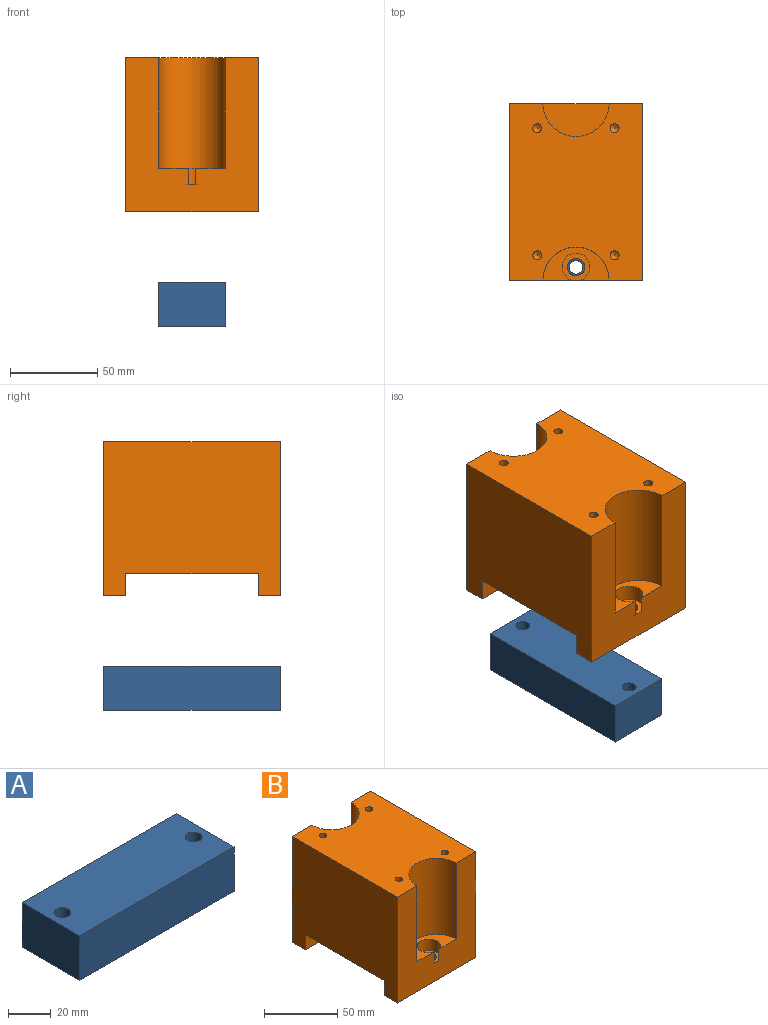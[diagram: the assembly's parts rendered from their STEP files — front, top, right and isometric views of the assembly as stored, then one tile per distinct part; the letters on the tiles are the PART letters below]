
ASSEMBLY  parts=2 mates=1
PART A: 8 faces, bbox 101.6x38.1x25.4 mm
  f0: plane 38.1x25.4mm, normal (-1,0,0), area 967.7mm2, adj f1,f3,f4,f5
  f1: plane 101.6x25.4mm, normal (0,-1,0), area 2580.6mm2, adj f0,f2,f4,f5
  f2: plane 38.1x25.4mm, normal (1,0,0), area 967.7mm2, adj f1,f3,f4,f5
  f3: plane 101.6x25.4mm, normal (0,1,0), area 2580.6mm2, adj f0,f2,f4,f5
  f4: plane 101.6x38.1mm, normal (0,0,1), area 3772mm2, adj f0,f1,f2,f3,f6,f7
  f5: plane 101.6x38.1mm, normal (0,0,-1), area 3772mm2, adj f0,f1,f2,f3,f6,f7
  f6: cylinder r=3.97mm len=25.4mm, axis (0,0,1), area 633.4mm2, adj f4,f5
  f7: cylinder r=3.97mm len=25.4mm, axis (0,0,1), area 633.4mm2, adj f4,f5
PART B: 25 faces, bbox 76.2x101.6x88.5 mm
  f0: plane 88.52x76.2mm, normal (0,-1,0), area 4283.5mm2, adj f1,f4,f5,f6,f9,f11,f14,f15
  f1: plane 38.1x19.05mm, normal (0,0,1), area 373.1mm2, adj f0,f9,f15
  f2: plane 76.2x76.2mm, normal (0,0,-1), area 5806.4mm2, adj f5,f6,f10,f12
  f3: plane 88.52x76.2mm, normal (0,1,0), area 4325.8mm2, adj f4,f5,f6,f7,f8,f13
  f4: plane 101.6x76.2mm, normal (0,0,1), area 6519.9mm2, adj f0,f3,f5,f6,f7,f9,f18,f20
  f5: plane 101.6x88.52mm, normal (-1,0,0), area 8025.8mm2, adj f0,f2,f3,f4,f10,f11,f12,f13
  f6: plane 101.6x88.52mm, normal (1,0,0), area 8025.8mm2, adj f0,f2,f3,f4,f10,f11,f12,f13
  f7: cylinder r=19.05mm len=63.5mm, axis (0,0,1), area 3800.3mm2, adj f3,f4,f8
  f8: plane 38.1x19.05mm, normal (0,0,1), area 570mm2, adj f3,f7
  f9: cylinder r=19.05mm len=63.5mm, axis (0,0,1), area 3800.3mm2, adj f0,f1,f4
  f10: plane 76.2x12.7mm, normal (0,1,0), area 967.7mm2, adj f2,f5,f6,f11
  f11: plane 76.2x12.7mm, normal (0,0,-1), area 887.9mm2, adj f0,f5,f6,f10,f16
  f12: plane 76.2x12.7mm, normal (0,-1,0), area 967.7mm2, adj f2,f5,f6,f13
  f13: plane 76.2x12.7mm, normal (0,0,-1), area 967.7mm2, adj f3,f5,f6,f12
  f14: plane 15.88x15.56mm, normal (0,0,1), area 117.1mm2, adj f0,f15,f16
  f15: cylinder r=7.94mm len=15.88mm, axis (0,0,1), area 432.1mm2, adj f0,f1,f14
  f16: cylinder r=5.04mm len=15.49mm, axis (0,0,1), area 490.8mm2, adj f11,f14
  f17: cone r=0mm half-angle=59deg, axis (0,0,1), area 23.9mm2, adj f18
  f18: cylinder r=2.55mm len=22.86mm, axis (0,0,1), area 366.7mm2, adj f4,f17
  f19: cone r=0mm half-angle=59deg, axis (0,0,1), area 23.9mm2, adj f20
  f20: cylinder r=2.55mm len=22.86mm, axis (0,0,1), area 366.7mm2, adj f4,f19
  f21: cone r=0mm half-angle=59deg, axis (0,0,1), area 23.9mm2, adj f22
  f22: cylinder r=2.55mm len=22.86mm, axis (0,0,1), area 366.7mm2, adj f4,f21
  f23: cone r=0mm half-angle=59deg, axis (0,0,1), area 23.9mm2, adj f24
  f24: cylinder r=2.55mm len=22.86mm, axis (0,0,1), area 366.7mm2, adj f4,f23
PLACE A rot(axis=(0.71,-0.71,0),180deg) t=(-22.34,148.75,-36.18)mm
PLACE B t=(-79.49,47.15,16.89)mm
MATE cylindrical A.f6 <-> B.f15  axis (0,0,1) through (-41.39,54.77,-36.18)mm
